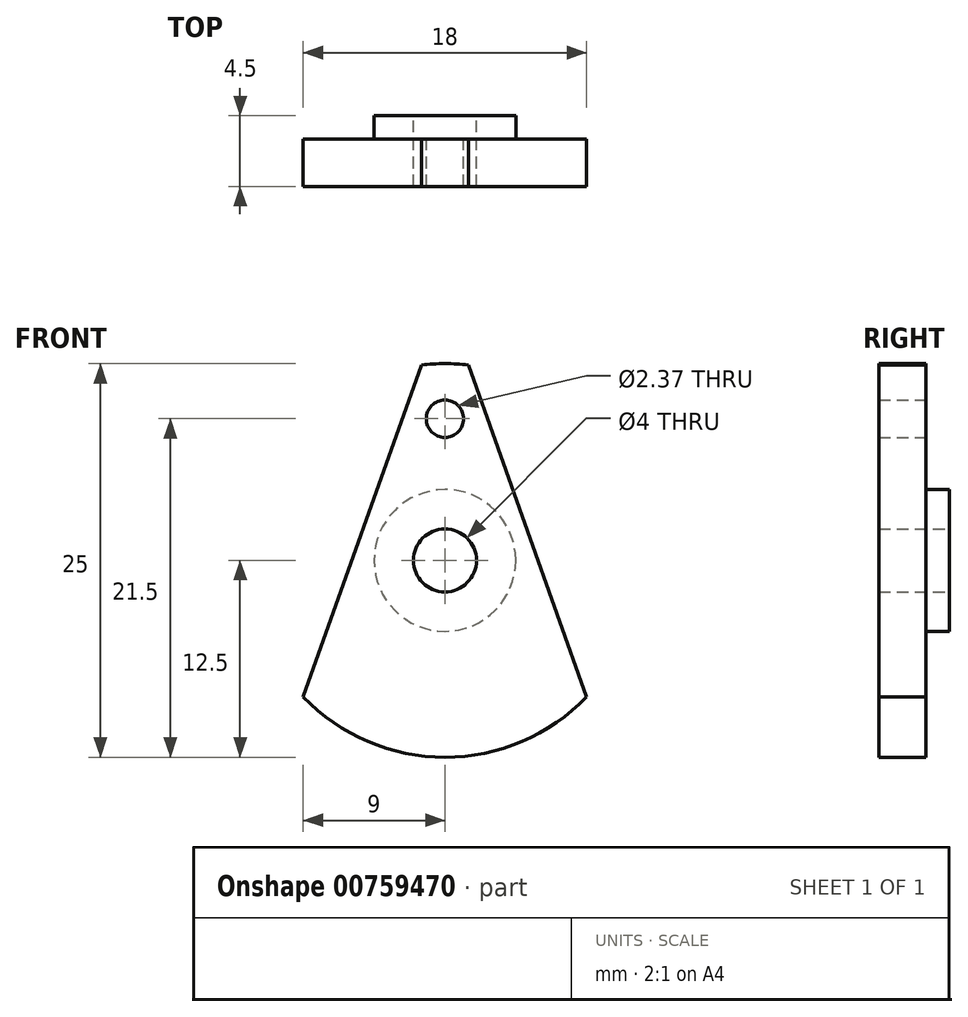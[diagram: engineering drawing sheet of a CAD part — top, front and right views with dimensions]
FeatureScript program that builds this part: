
annotation { "Feature Type Name" : "Feature", "Feature Type Description" : "" }
export const myFeature = defineFeature(function(context is Context, id is Id, definition is map)
    precondition{}
    {
        {
            var Q0;
            Q0=qCreatedBy(makeId("Front.planeOp"),FACE);
            var sketch = newSketch(context, id + "F0", { "sketchPlane" : qUnion([Q0])});
            skArc(sketch, "E0", {"start": v(-9, -8.67) * mm, "mid": v(0, -12.5) * mm, "end": v(9, -8.67) * mm});
            skLineSegment(sketch, "E1", {"start": v(1.5, 12.4) * mm, "end": v(9, -8.67) * mm});
            skLineSegment(sketch, "E2.MirrorCS", {"start": v(-1.5, 12.4) * mm, "end": v(-9, -8.67) * mm});
            skArc(sketch, "E3.trimOffspring", {"start": v(1.5, 12.4) * mm, "mid": v(0, 12.5) * mm, "end": v(-1.5, 12.4) * mm});
            skCircle(sketch, "E4", {"center": v(0, 0) * mm, "radius": 2 * mm});
            skCircle(sketch, "E5", {"center": v(0, 0) * mm, "radius": 4.5 * mm});
            skCircle(sketch, "E6", {"center": v(0, 9) * mm, "radius": 1.19 * mm});
            skSolve(sketch);
        }
        {
            var Q0;
            Q0 = qSketchRegion(id + "F0", true);
            var Q1;
            Q1=makeQuery(id+"F0.imprint","IMPRINT",FACE,{"disambiguationData":[TD([[makeQuery(id+"F0.imprint","IMPRINT",EDGE,{"derivedFrom":sQuery(id+"F0.wireOp",EDGE,"E4")}),-1.0]])]});
            extrude(context, id + "F1", {"entities" : qUnion([Q0, Q1]), "depth" : 3 * mm, "offsetDistance" : 25 * mm});
        }
        {
            var Q0;
            Q0=makeQuery(id+"F0.imprint","IMPRINT",FACE,{"disambiguationData":[TD([[makeQuery(id+"F0.imprint","IMPRINT",EDGE,{"derivedFrom":sQuery(id+"F0.wireOp",EDGE,"E4")}),-1.0]])]});
            extrude(context, id + "F2", {"entities" : qUnion([Q0]), "operationType" : NewBodyOperationType.ADD, "oppositeDirection" : true, "depth" : 1.5 * mm, "offsetDistance" : 25 * mm});
        }
    });
